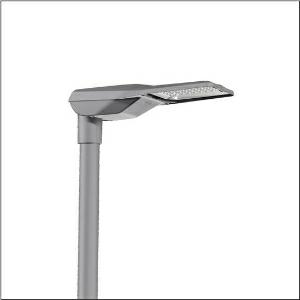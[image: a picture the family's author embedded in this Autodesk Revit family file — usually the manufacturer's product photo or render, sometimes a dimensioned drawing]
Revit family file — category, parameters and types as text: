
# Revit family: streetlight_sl_21_iq_mini___stw1_0a_5xe2e61d08hb_c7c8
name_source: partatom
category: Lighting Fixtures
units: mm (PartAtom-declared; Revit-internal decimal feet)

## family parameters
Cut with Voids When Loaded = No
Host = Face
Light Source = No
Part Type = Normal
Room Calculation Point = No
Round Connector Dimension = Use Diameter
Shared = No

## types (1)
- --- (1 x LED, 8480 lm, 70.9 W, 2700K)
    Apparent Load = 71 VA
    CIE Flux Codes = 38 75 98 100 100
    Color Rendering = 70
    Color Temperature = 2700K
    Default Elevation = 1800 mm
    Description = Streetlight SL 21 iQ mini, mast luminaire, primary light control with lens, of PMMA, primary optical cover: cover, of toughened safety glass, transparent, light distribution: STW1.0a, light emission: direct distribution, primary light characteristic: asymmetric, installation type: post-top, side-entry, LED, High Power LED, rated luminous flux: 8.480lm, luminous efficacy: 120lm/W, light colour: 727, colour temperature: 2700K, control gear: iQ-Comfort, control: Auto-Match, Temp-Guard, Lumen-Switch, Night-Set, Smart-Wire, Light-Fading, Desk-Remote (wireless, voltage-free reading and setting of iQ features in the workshop via application-optimized NFC function/RFID function), optimised constant luminous flux control (CLO 2.0), pre-setting: linear dimming characteristic, mains connection: 220..240V, AC, 50/60Hz, start of lifetime: 71W, end of service life: 75W, reduction: 31W, luminaire housing, of diecast aluminium, powder-coated, Siteco® metallic grey (DB 702S), corrosivity category C5 mid according to DIN EN ISO 12944, please order mast flange separately, inclination adjustable: 0°, 5°, 10°, 15°, sealing non-destructively replaceable, multi-level sealing system, length: 628mm, width: 235mm, height: 110mm, mast flange for spigot size: 42mm (side-entry): 5XC10008XM4, 60/48mm (side-entry/post-top): 5XC10108XM2, 76/60mm (side-entry/post-top): 5XC10108XM1, mounting height: 4..8m, protection rating (complete): IP66, insulation class (complete): insulation class II (safety insulation), certification: CE, ENEC, ENEC+, VDE, impact resistance: IK10, permissible operating ambient temperature for outdoor applications: -40..+50°C, standard-compliant lighting for roads and squares, packaging unit: 1 piece

Light Distribution: STW1.0a
    Height = 110 mm
    Lamp = 1 x LED
    Lamp Light Flux = 8480 lm
    Lamp Power = 70.9 W
    Lamp count = 1
    Length = 625 mm
    Luminous efficacy = 120 lm/W
    Manufacturer = Siteco
    ModVariant = No
    Model = 5XE2E61D08HB
    Number of Poles = 1
    OnlyDefault = Yes
    Power Factor = 1
    Product Name = Streetlight SL 21 iQ mini | STW1.0a
    Product group = mast luminaire | pylon top
    ProductGroupID = 6100
    Protection Class = Protection class II
    Protection Degree = IP 66
    RLX_Detail_Level = 1
    RLX_Emergency_Light_Flux = 0 lm
    RLX_Emergency_Type = 0
    RLX_Emergency_Type_DB = No
    RlxData = <blob elided: 26345 chars, md5=0e6d773d>
    Socket = socket
    Standby Power = 0 W
    System Light Flux = 8480 lm
    System Power = 71 W
    Type Comments = factory setting: luminous flux: 100 % | dim-lin: 254 | 711 mA
    Type Image = l_1003519.jpg
    URL = http://relux.com
    VarID = @adj_179401
    Voltage = 0 V
    Weight = 0.00 kg
    Width = 234 mm

## geometry (parser evidence)
native form markers: Blend x4, Sweep x10
no freeform markers — native parametric forms only
